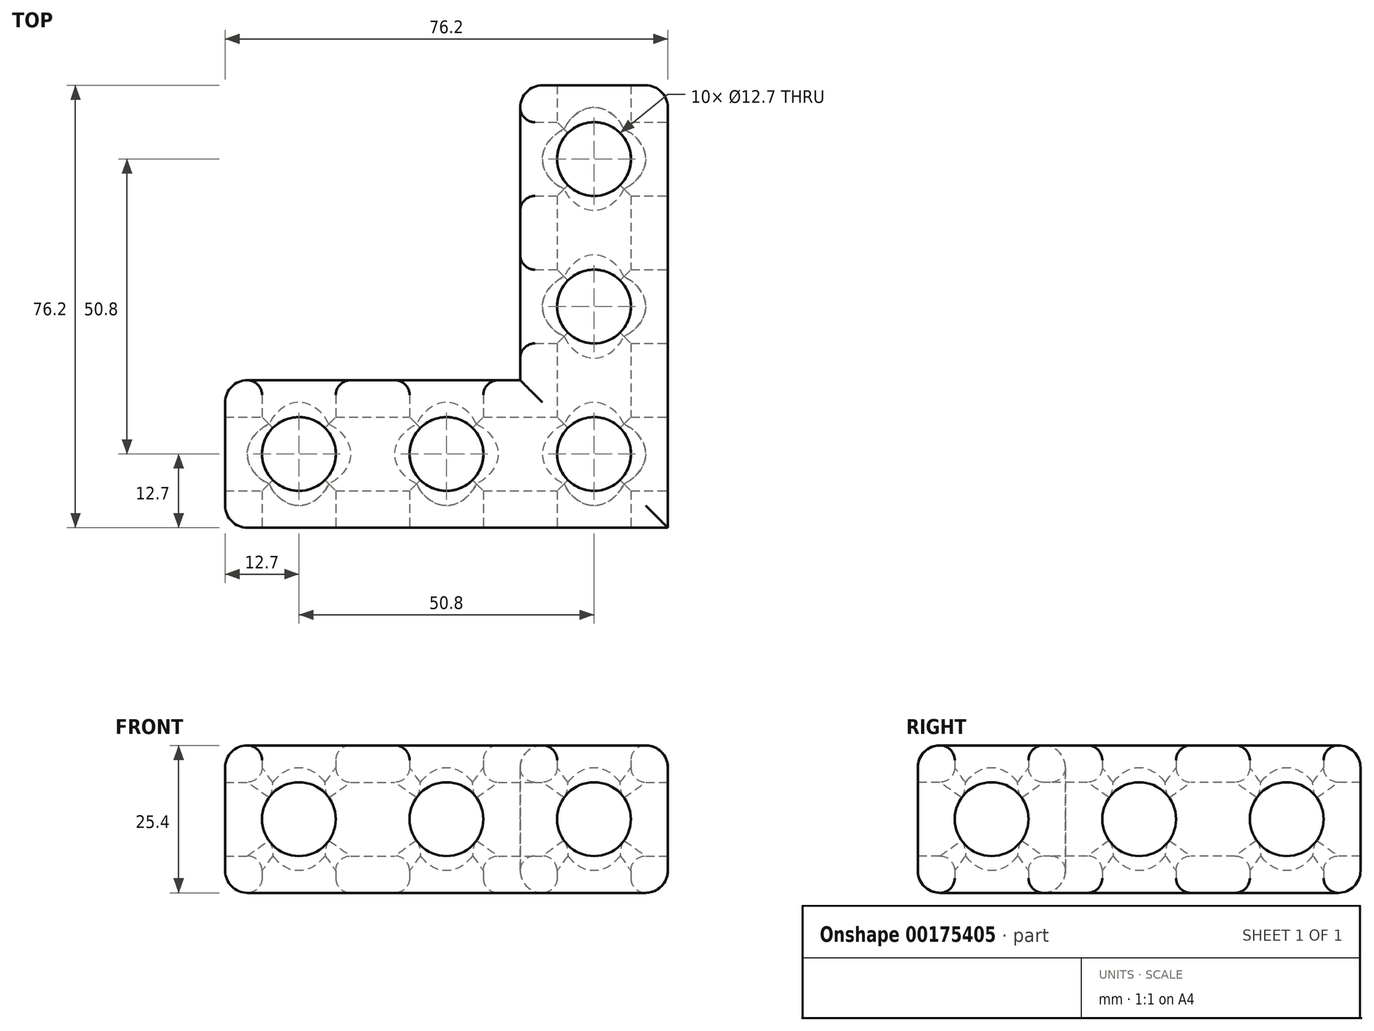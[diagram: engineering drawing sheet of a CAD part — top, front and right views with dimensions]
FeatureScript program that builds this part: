
annotation { "Feature Type Name" : "Feature", "Feature Type Description" : "" }
export const myFeature = defineFeature(function(context is Context, id is Id, definition is map)
    precondition{}
    {
        {
            var Q0;
            Q0=qCreatedBy(makeId("Top.planeOp"),FACE);
            var sketch = newSketch(context, id + "F0", { "sketchPlane" : qUnion([Q0])});
            skLineSegment(sketch, "E0.bottom", {"start": v(0, 0) * mm, "end": v(76.2, 0) * mm});
            skLineSegment(sketch, "E0.left", {"start": v(0, 0) * mm, "end": v(0, 25.4) * mm});
            skLineSegment(sketch, "E0.right", {"start": v(76.2, 0) * mm, "end": v(76.2, 18.8) * mm});
            skLineSegment(sketch, "E1.bottom", {"start": v(76.2, 0) * mm, "end": v(57.4, 0) * mm});
            skLineSegment(sketch, "E1.top", {"start": v(76.2, 76.2) * mm, "end": v(50.8, 76.2) * mm});
            skLineSegment(sketch, "E1.left", {"start": v(76.2, 0) * mm, "end": v(76.2, 76.2) * mm});
            skLineSegment(sketch, "E2", {"start": v(50.8, 76.2) * mm, "end": v(50.8, 25.4) * mm});
            skLineSegment(sketch, "E3", {"start": v(0, 25.4) * mm, "end": v(50.8, 25.4) * mm});
            skCircle(sketch, "E4", {"center": v(12.7, 12.7) * mm, "radius": 6.35 * mm});
            skCircle(sketch, "E5", {"center": v(38.1, 12.7) * mm, "radius": 6.35 * mm});
            skCircle(sketch, "E6", {"center": v(63.5, 12.7) * mm, "radius": 6.35 * mm});
            skCircle(sketch, "E7", {"center": v(63.5, 38.1) * mm, "radius": 6.35 * mm});
            skCircle(sketch, "E8", {"center": v(63.5, 63.5) * mm, "radius": 6.35 * mm});
            skSolve(sketch);
        }
        {
            var Q0;
            Q0=qSketchRegion(id+"F0",true);
            extrude(context, id + "F1", {"entities" : qUnion([Q0]), "depth" : 25.4 * mm});
        }
        {
            var Q0;
            Q0=makeQuery(id+"F1.opExtrude","SWEPT_FACE",FACE,{"disambiguationData":[OSD([sQuery(id+"F0.wireOp",EDGE,"E0.bottom"),sQuery(id+"F0.wireOp",EDGE,"E1.bottom")])]});
            var sketch = newSketch(context, id + "F2", { "sketchPlane" : qUnion([Q0])});
            skCircle(sketch, "E9", {"center": v(12.7, 12.7) * mm, "radius": 6.35 * mm});
            skCircle(sketch, "E10", {"center": v(38.1, 12.7) * mm, "radius": 6.35 * mm});
            skCircle(sketch, "E11", {"center": v(63.5, 12.7) * mm, "radius": 6.35 * mm});
            skSolve(sketch);
        }
        {
            var Q0;
            Q0=qSketchRegion(id+"F2",true);
            extrude(context, id + "F3", {"entities" : qUnion([Q0]), "operationType" : NewBodyOperationType.REMOVE, "oppositeDirection" : true, "depth" : 76.2 * mm});
        }
        {
            var Q0;
            Q0=makeQuery(id+"F1.opExtrude","SWEPT_FACE",FACE,{"disambiguationData":[OSD([sQuery(id+"F0.wireOp",EDGE,"E1.left")])]});
            var sketch = newSketch(context, id + "F4", { "sketchPlane" : qUnion([Q0])});
            skLineSegment(sketch, "E12.bottom", {"start": v(0, 0) * mm, "end": v(25.4, 0) * mm});
            skLineSegment(sketch, "E12.top", {"start": v(0, 25.4) * mm, "end": v(25.4, 25.4) * mm});
            skLineSegment(sketch, "E12.left", {"start": v(0, 0) * mm, "end": v(0, 25.4) * mm});
            skLineSegment(sketch, "E13.bottom", {"start": v(25.4, 0) * mm, "end": v(50.8, 0) * mm});
            skLineSegment(sketch, "E13.top", {"start": v(25.4, 25.4) * mm, "end": v(50.8, 25.4) * mm});
            skLineSegment(sketch, "E14.bottom", {"start": v(50.8, 0) * mm, "end": v(76.2, 0) * mm});
            skLineSegment(sketch, "E14.top", {"start": v(50.8, 25.4) * mm, "end": v(76.2, 25.4) * mm});
            skLineSegment(sketch, "E14.right", {"start": v(76.2, 0) * mm, "end": v(76.2, 25.4) * mm});
            skCircle(sketch, "E15", {"center": v(12.7, 12.7) * mm, "radius": 6.35 * mm});
            skCircle(sketch, "E16", {"center": v(38.1, 12.7) * mm, "radius": 6.35 * mm});
            skCircle(sketch, "E17", {"center": v(63.5, 12.7) * mm, "radius": 6.35 * mm});
            skSolve(sketch);
        }
        {
            var Q0;
            Q0=makeQuery(id+"F4.imprint","IMPRINT",FACE,{"disambiguationData":[TD([[makeQuery(id+"F4.imprint","IMPRINT",EDGE,{"derivedFrom":sQuery(id+"F4.wireOp",EDGE,"E15")}),1.0]])]});
            var Q1;
            Q1=makeQuery(id+"F4.imprint","IMPRINT",FACE,{"disambiguationData":[TD([[makeQuery(id+"F4.imprint","IMPRINT",EDGE,{"derivedFrom":sQuery(id+"F4.wireOp",EDGE,"E16")}),1.0]])]});
            var Q2;
            Q2=makeQuery(id+"F4.imprint","IMPRINT",FACE,{"disambiguationData":[TD([[makeQuery(id+"F4.imprint","IMPRINT",EDGE,{"derivedFrom":sQuery(id+"F4.wireOp",EDGE,"E17")}),1.0]])]});
            extrude(context, id + "F5", {"entities" : qUnion([Q0, Q1, Q2]), "operationType" : NewBodyOperationType.REMOVE, "oppositeDirection" : true, "depth" : 76.2 * mm});
        }
        {
            var Q0;
            Q0=makeQuery(id+"F1.opExtrude","CAP_EDGE",EDGE,{"disambiguationData":[OSD([sQuery(id+"F0.wireOp",EDGE,"E0.bottom"),sQuery(id+"F0.wireOp",EDGE,"E1.bottom")])],"isStart":false});
            var Q1;
            Q1=makeQuery(id+"F1.opExtrude","CAP_EDGE",EDGE,{"disambiguationData":[OSD([sQuery(id+"F0.wireOp",EDGE,"E1.left")])],"isStart":false});
            var Q2;
            Q2=makeQuery(id+"F1.opExtrude","CAP_EDGE",EDGE,{"disambiguationData":[OSD([sQuery(id+"F0.wireOp",EDGE,"E3")])],"isStart":false});
            var Q3;
            Q3=makeQuery(id+"F1.opExtrude","CAP_EDGE",EDGE,{"disambiguationData":[OSD([sQuery(id+"F0.wireOp",EDGE,"E2")])],"isStart":false});
            var Q4;
            Q4=makeQuery(id+"F1.opExtrude","SWEPT_EDGE",EDGE,{"disambiguationData":[OSD([sQuery(id+"F0.wireOp",EDGE,"E0.bottom"),sQuery(id+"F0.wireOp",EDGE,"E0.left")])]});
            var Q5;
            Q5=makeQuery(id+"F1.opExtrude","CAP_EDGE",EDGE,{"disambiguationData":[OSD([sQuery(id+"F0.wireOp",EDGE,"E0.bottom"),sQuery(id+"F0.wireOp",EDGE,"E1.bottom")])],"isStart":true});
            var Q6;
            Q6=makeQuery(id+"F1.opExtrude","CAP_EDGE",EDGE,{"disambiguationData":[OSD([sQuery(id+"F0.wireOp",EDGE,"E1.left")])],"isStart":true});
            var Q7;
            Q7=makeQuery(id+"F1.opExtrude","SWEPT_EDGE",EDGE,{"disambiguationData":[OSD([sQuery(id+"F0.wireOp",EDGE,"E1.bottom"),sQuery(id+"F0.wireOp",EDGE,"E1.left")])]});
            var Q8;
            Q8=makeQuery(id+"F1.opExtrude","CAP_EDGE",EDGE,{"disambiguationData":[OSD([sQuery(id+"F0.wireOp",EDGE,"E0.left")])],"isStart":false});
            var Q9;
            Q9=makeQuery(id+"F1.opExtrude","CAP_EDGE",EDGE,{"disambiguationData":[OSD([sQuery(id+"F0.wireOp",EDGE,"E0.left")])],"isStart":true});
            var Q10;
            Q10=makeQuery(id+"F1.opExtrude","SWEPT_EDGE",EDGE,{"disambiguationData":[OSD([sQuery(id+"F0.wireOp",EDGE,"E0.left"),sQuery(id+"F0.wireOp",EDGE,"E3")])]});
            var Q11;
            Q11=makeQuery(id+"F1.opExtrude","CAP_EDGE",EDGE,{"disambiguationData":[OSD([sQuery(id+"F0.wireOp",EDGE,"E3")])],"isStart":true});
            var Q12;
            Q12=makeQuery(id+"F1.opExtrude","SWEPT_EDGE",EDGE,{"disambiguationData":[OSD([sQuery(id+"F0.wireOp",EDGE,"E1.top"),sQuery(id+"F0.wireOp",EDGE,"E2")])]});
            var Q13;
            Q13=makeQuery(id+"F1.opExtrude","CAP_EDGE",EDGE,{"disambiguationData":[OSD([sQuery(id+"F0.wireOp",EDGE,"E2")])],"isStart":true});
            var Q14;
            Q14=makeQuery(id+"F1.opExtrude","CAP_EDGE",EDGE,{"disambiguationData":[OSD([sQuery(id+"F0.wireOp",EDGE,"E1.top")])],"isStart":true});
            var Q15;
            Q15=makeQuery(id+"F1.opExtrude","SWEPT_EDGE",EDGE,{"disambiguationData":[OSD([sQuery(id+"F0.wireOp",EDGE,"E1.top"),sQuery(id+"F0.wireOp",EDGE,"E1.left")])]});
            var Q16;
            Q16=makeQuery(id+"F1.opExtrude","CAP_EDGE",EDGE,{"disambiguationData":[OSD([sQuery(id+"F0.wireOp",EDGE,"E1.top")])],"isStart":false});
            fillet(context, id + "F6", {"entities" : qUnion([Q0, Q1, Q2, Q3, Q4, Q5, Q6, Q7, Q8, Q9, Q10, Q11, Q12, Q13, Q14, Q15, Q16]), "radius" : 3.8 * mm, "allowEdgeOverflow" : false});
        }
        {
            var Q0;
            {var subQ0=sQuery(id+"F0.wireOp",EDGE,"E4");var subQ1=makeQuery(id+"F1.opExtrude","SWEPT_FACE",FACE,{"disambiguationData":[OSD([subQ0])]});Q0=makeQuery(id+"F5.boolean.opBoolean","INTERSECT",EDGE,{"disambiguationData":[OD(0.0)],"derivedFrom":[makeQuery(id+"F3.boolean.opBoolean","SPLIT",FACE,{"disambiguationData":[TD([makeQuery(id+"F1.opExtrude","CAP_FACE",FACE,{"disambiguationData":[OSD([sQuery(id+"F0.wireOp",EDGE,"E0.bottom"),sQuery(id+"F0.wireOp",EDGE,"E0.left"),sQuery(id+"F0.wireOp",EDGE,"E1.bottom"),sQuery(id+"F0.wireOp",EDGE,"E1.top"),sQuery(id+"F0.wireOp",EDGE,"E1.left"),sQuery(id+"F0.wireOp",EDGE,"E2"),sQuery(id+"F0.wireOp",EDGE,"E3"),subQ0,sQuery(id+"F0.wireOp",EDGE,"E5"),sQuery(id+"F0.wireOp",EDGE,"E6"),sQuery(id+"F0.wireOp",EDGE,"E7"),sQuery(id+"F0.wireOp",EDGE,"E8")])],"isStart":true})])],"derivedFrom":subQ1}),makeQuery(id+"F5.opExtrude","SWEPT_FACE",FACE,{"disambiguationData":[OSD([sQuery(id+"F4.wireOp",EDGE,"E15")])]})]});}
            var Q1;
            Q1=makeQuery(id+"F3.boolean.opBoolean","INTERSECT",EDGE,{"disambiguationData":[OD(0.0)],"derivedFrom":[makeQuery(id+"F1.opExtrude","SWEPT_FACE",FACE,{"disambiguationData":[OSD([sQuery(id+"F0.wireOp",EDGE,"E4")])]}),makeQuery(id+"F3.opExtrude","SWEPT_FACE",FACE,{"disambiguationData":[OSD([sQuery(id+"F2.wireOp",EDGE,"E9")])]})]});
            var Q2;
            Q2=makeQuery(id+"F5.boolean.opBoolean","INTERSECT",EDGE,{"disambiguationData":[OD(0.0)],"derivedFrom":[makeQuery(id+"F3.boolean.opBoolean","COPY",FACE,{"disambiguationData":[OD(0.0)],"derivedFrom":makeQuery(id+"F3.opExtrude","SWEPT_FACE",FACE,{"disambiguationData":[OSD([sQuery(id+"F2.wireOp",EDGE,"E9")])]})}),makeQuery(id+"F5.opExtrude","SWEPT_FACE",FACE,{"disambiguationData":[OSD([sQuery(id+"F4.wireOp",EDGE,"E15")])]})]});
            var Q3;
            Q3=makeQuery(id+"F5.boolean.opBoolean","INTERSECT",EDGE,{"disambiguationData":[OD(0.0)],"derivedFrom":[makeQuery(id+"F3.boolean.opBoolean","COPY",FACE,{"disambiguationData":[OD(1.0)],"derivedFrom":makeQuery(id+"F3.opExtrude","SWEPT_FACE",FACE,{"disambiguationData":[OSD([sQuery(id+"F2.wireOp",EDGE,"E9")])]})}),makeQuery(id+"F5.opExtrude","SWEPT_FACE",FACE,{"disambiguationData":[OSD([sQuery(id+"F4.wireOp",EDGE,"E15")])]})]});
            var Q4;
            {var subQ0=sQuery(id+"F0.wireOp",EDGE,"E4");var subQ1=makeQuery(id+"F1.opExtrude","SWEPT_FACE",FACE,{"disambiguationData":[OSD([subQ0])]});Q4=makeQuery(id+"F5.boolean.opBoolean","INTERSECT",EDGE,{"disambiguationData":[OD(0.0)],"derivedFrom":[makeQuery(id+"F3.boolean.opBoolean","SPLIT",FACE,{"disambiguationData":[TD([makeQuery(id+"F1.opExtrude","CAP_FACE",FACE,{"disambiguationData":[OSD([sQuery(id+"F0.wireOp",EDGE,"E0.bottom"),sQuery(id+"F0.wireOp",EDGE,"E0.left"),sQuery(id+"F0.wireOp",EDGE,"E1.bottom"),sQuery(id+"F0.wireOp",EDGE,"E1.top"),sQuery(id+"F0.wireOp",EDGE,"E1.left"),sQuery(id+"F0.wireOp",EDGE,"E2"),sQuery(id+"F0.wireOp",EDGE,"E3"),subQ0,sQuery(id+"F0.wireOp",EDGE,"E5"),sQuery(id+"F0.wireOp",EDGE,"E6"),sQuery(id+"F0.wireOp",EDGE,"E7"),sQuery(id+"F0.wireOp",EDGE,"E8")])],"isStart":false})])],"derivedFrom":subQ1}),makeQuery(id+"F5.opExtrude","SWEPT_FACE",FACE,{"disambiguationData":[OSD([sQuery(id+"F4.wireOp",EDGE,"E15")])]})]});}
            var Q5;
            Q5=makeQuery(id+"F3.boolean.opBoolean","INTERSECT",EDGE,{"disambiguationData":[OD(3.0)],"derivedFrom":[makeQuery(id+"F1.opExtrude","SWEPT_FACE",FACE,{"disambiguationData":[OSD([sQuery(id+"F0.wireOp",EDGE,"E4")])]}),makeQuery(id+"F3.opExtrude","SWEPT_FACE",FACE,{"disambiguationData":[OSD([sQuery(id+"F2.wireOp",EDGE,"E9")])]})]});
            var Q6;
            Q6=makeQuery(id+"F3.boolean.opBoolean","INTERSECT",EDGE,{"disambiguationData":[OD(1.0)],"derivedFrom":[makeQuery(id+"F1.opExtrude","SWEPT_FACE",FACE,{"disambiguationData":[OSD([sQuery(id+"F0.wireOp",EDGE,"E4")])]}),makeQuery(id+"F3.opExtrude","SWEPT_FACE",FACE,{"disambiguationData":[OSD([sQuery(id+"F2.wireOp",EDGE,"E9")])]})]});
            var Q7;
            {var subQ0=sQuery(id+"F0.wireOp",EDGE,"E4");var subQ1=makeQuery(id+"F1.opExtrude","SWEPT_FACE",FACE,{"disambiguationData":[OSD([subQ0])]});Q7=makeQuery(id+"F5.boolean.opBoolean","INTERSECT",EDGE,{"disambiguationData":[OD(1.0)],"derivedFrom":[makeQuery(id+"F3.boolean.opBoolean","SPLIT",FACE,{"disambiguationData":[TD([makeQuery(id+"F1.opExtrude","CAP_FACE",FACE,{"disambiguationData":[OSD([sQuery(id+"F0.wireOp",EDGE,"E0.bottom"),sQuery(id+"F0.wireOp",EDGE,"E0.left"),sQuery(id+"F0.wireOp",EDGE,"E1.bottom"),sQuery(id+"F0.wireOp",EDGE,"E1.top"),sQuery(id+"F0.wireOp",EDGE,"E1.left"),sQuery(id+"F0.wireOp",EDGE,"E2"),sQuery(id+"F0.wireOp",EDGE,"E3"),subQ0,sQuery(id+"F0.wireOp",EDGE,"E5"),sQuery(id+"F0.wireOp",EDGE,"E6"),sQuery(id+"F0.wireOp",EDGE,"E7"),sQuery(id+"F0.wireOp",EDGE,"E8")])],"isStart":true})])],"derivedFrom":subQ1}),makeQuery(id+"F5.opExtrude","SWEPT_FACE",FACE,{"disambiguationData":[OSD([sQuery(id+"F4.wireOp",EDGE,"E15")])]})]});}
            var Q8;
            Q8=makeQuery(id+"F5.boolean.opBoolean","INTERSECT",EDGE,{"disambiguationData":[OD(1.0)],"derivedFrom":[makeQuery(id+"F3.boolean.opBoolean","COPY",FACE,{"disambiguationData":[OD(0.0)],"derivedFrom":makeQuery(id+"F3.opExtrude","SWEPT_FACE",FACE,{"disambiguationData":[OSD([sQuery(id+"F2.wireOp",EDGE,"E9")])]})}),makeQuery(id+"F5.opExtrude","SWEPT_FACE",FACE,{"disambiguationData":[OSD([sQuery(id+"F4.wireOp",EDGE,"E15")])]})]});
            var Q9;
            Q9=makeQuery(id+"F3.boolean.opBoolean","INTERSECT",EDGE,{"disambiguationData":[OD(2.0)],"derivedFrom":[makeQuery(id+"F1.opExtrude","SWEPT_FACE",FACE,{"disambiguationData":[OSD([sQuery(id+"F0.wireOp",EDGE,"E4")])]}),makeQuery(id+"F3.opExtrude","SWEPT_FACE",FACE,{"disambiguationData":[OSD([sQuery(id+"F2.wireOp",EDGE,"E9")])]})]});
            var Q10;
            {var subQ0=sQuery(id+"F0.wireOp",EDGE,"E4");var subQ1=makeQuery(id+"F1.opExtrude","SWEPT_FACE",FACE,{"disambiguationData":[OSD([subQ0])]});Q10=makeQuery(id+"F5.boolean.opBoolean","INTERSECT",EDGE,{"disambiguationData":[OD(1.0)],"derivedFrom":[makeQuery(id+"F3.boolean.opBoolean","SPLIT",FACE,{"disambiguationData":[TD([makeQuery(id+"F1.opExtrude","CAP_FACE",FACE,{"disambiguationData":[OSD([sQuery(id+"F0.wireOp",EDGE,"E0.bottom"),sQuery(id+"F0.wireOp",EDGE,"E0.left"),sQuery(id+"F0.wireOp",EDGE,"E1.bottom"),sQuery(id+"F0.wireOp",EDGE,"E1.top"),sQuery(id+"F0.wireOp",EDGE,"E1.left"),sQuery(id+"F0.wireOp",EDGE,"E2"),sQuery(id+"F0.wireOp",EDGE,"E3"),subQ0,sQuery(id+"F0.wireOp",EDGE,"E5"),sQuery(id+"F0.wireOp",EDGE,"E6"),sQuery(id+"F0.wireOp",EDGE,"E7"),sQuery(id+"F0.wireOp",EDGE,"E8")])],"isStart":false})])],"derivedFrom":subQ1}),makeQuery(id+"F5.opExtrude","SWEPT_FACE",FACE,{"disambiguationData":[OSD([sQuery(id+"F4.wireOp",EDGE,"E15")])]})]});}
            var Q11;
            Q11=makeQuery(id+"F5.boolean.opBoolean","INTERSECT",EDGE,{"disambiguationData":[OD(1.0)],"derivedFrom":[makeQuery(id+"F3.boolean.opBoolean","COPY",FACE,{"disambiguationData":[OD(1.0)],"derivedFrom":makeQuery(id+"F3.opExtrude","SWEPT_FACE",FACE,{"disambiguationData":[OSD([sQuery(id+"F2.wireOp",EDGE,"E9")])]})}),makeQuery(id+"F5.opExtrude","SWEPT_FACE",FACE,{"disambiguationData":[OSD([sQuery(id+"F4.wireOp",EDGE,"E15")])]})]});
            fillet(context, id + "F7", {"entities" : qUnion([Q0, Q1, Q2, Q3, Q4, Q5, Q6, Q7, Q8, Q9, Q10, Q11]), "radius" : 2.54 * mm, "tangentPropagation" : true, "allowEdgeOverflow" : false});
        }
        {
            var Q0;
            {var subQ0=sQuery(id+"F0.wireOp",EDGE,"E5");var subQ1=makeQuery(id+"F1.opExtrude","SWEPT_FACE",FACE,{"disambiguationData":[OSD([subQ0])]});Q0=makeQuery(id+"F5.boolean.opBoolean","INTERSECT",EDGE,{"disambiguationData":[OD(0.0)],"derivedFrom":[makeQuery(id+"F3.boolean.opBoolean","SPLIT",FACE,{"disambiguationData":[TD([makeQuery(id+"F1.opExtrude","CAP_FACE",FACE,{"disambiguationData":[OSD([sQuery(id+"F0.wireOp",EDGE,"E0.bottom"),sQuery(id+"F0.wireOp",EDGE,"E0.left"),sQuery(id+"F0.wireOp",EDGE,"E1.bottom"),sQuery(id+"F0.wireOp",EDGE,"E1.top"),sQuery(id+"F0.wireOp",EDGE,"E1.left"),sQuery(id+"F0.wireOp",EDGE,"E2"),sQuery(id+"F0.wireOp",EDGE,"E3"),sQuery(id+"F0.wireOp",EDGE,"E4"),subQ0,sQuery(id+"F0.wireOp",EDGE,"E6"),sQuery(id+"F0.wireOp",EDGE,"E7"),sQuery(id+"F0.wireOp",EDGE,"E8")])],"isStart":true})])],"derivedFrom":subQ1}),makeQuery(id+"F5.opExtrude","SWEPT_FACE",FACE,{"disambiguationData":[OSD([sQuery(id+"F4.wireOp",EDGE,"E15")])]})]});}
            var Q1;
            Q1=makeQuery(id+"F3.boolean.opBoolean","INTERSECT",EDGE,{"disambiguationData":[OD(0.0)],"derivedFrom":[makeQuery(id+"F1.opExtrude","SWEPT_FACE",FACE,{"disambiguationData":[OSD([sQuery(id+"F0.wireOp",EDGE,"E5")])]}),makeQuery(id+"F3.opExtrude","SWEPT_FACE",FACE,{"disambiguationData":[OSD([sQuery(id+"F2.wireOp",EDGE,"E10")])]})]});
            var Q2;
            Q2=makeQuery(id+"F3.boolean.opBoolean","INTERSECT",EDGE,{"disambiguationData":[OD(1.0)],"derivedFrom":[makeQuery(id+"F1.opExtrude","SWEPT_FACE",FACE,{"disambiguationData":[OSD([sQuery(id+"F0.wireOp",EDGE,"E5")])]}),makeQuery(id+"F3.opExtrude","SWEPT_FACE",FACE,{"disambiguationData":[OSD([sQuery(id+"F2.wireOp",EDGE,"E10")])]})]});
            var Q3;
            {var subQ0=sQuery(id+"F0.wireOp",EDGE,"E5");var subQ1=makeQuery(id+"F1.opExtrude","SWEPT_FACE",FACE,{"disambiguationData":[OSD([subQ0])]});Q3=makeQuery(id+"F5.boolean.opBoolean","INTERSECT",EDGE,{"disambiguationData":[OD(1.0)],"derivedFrom":[makeQuery(id+"F3.boolean.opBoolean","SPLIT",FACE,{"disambiguationData":[TD([makeQuery(id+"F1.opExtrude","CAP_FACE",FACE,{"disambiguationData":[OSD([sQuery(id+"F0.wireOp",EDGE,"E0.bottom"),sQuery(id+"F0.wireOp",EDGE,"E0.left"),sQuery(id+"F0.wireOp",EDGE,"E1.bottom"),sQuery(id+"F0.wireOp",EDGE,"E1.top"),sQuery(id+"F0.wireOp",EDGE,"E1.left"),sQuery(id+"F0.wireOp",EDGE,"E2"),sQuery(id+"F0.wireOp",EDGE,"E3"),sQuery(id+"F0.wireOp",EDGE,"E4"),subQ0,sQuery(id+"F0.wireOp",EDGE,"E6"),sQuery(id+"F0.wireOp",EDGE,"E7"),sQuery(id+"F0.wireOp",EDGE,"E8")])],"isStart":true})])],"derivedFrom":subQ1}),makeQuery(id+"F5.opExtrude","SWEPT_FACE",FACE,{"disambiguationData":[OSD([sQuery(id+"F4.wireOp",EDGE,"E15")])]})]});}
            var Q4;
            Q4=makeQuery(id+"F5.boolean.opBoolean","INTERSECT",EDGE,{"disambiguationData":[OD(0.0)],"derivedFrom":[makeQuery(id+"F3.boolean.opBoolean","COPY",FACE,{"disambiguationData":[OD(0.0)],"derivedFrom":makeQuery(id+"F3.opExtrude","SWEPT_FACE",FACE,{"disambiguationData":[OSD([sQuery(id+"F2.wireOp",EDGE,"E10")])]})}),makeQuery(id+"F5.opExtrude","SWEPT_FACE",FACE,{"disambiguationData":[OSD([sQuery(id+"F4.wireOp",EDGE,"E15")])]})]});
            var Q5;
            Q5=makeQuery(id+"F5.boolean.opBoolean","INTERSECT",EDGE,{"disambiguationData":[OD(0.0)],"derivedFrom":[makeQuery(id+"F3.boolean.opBoolean","COPY",FACE,{"disambiguationData":[OD(1.0)],"derivedFrom":makeQuery(id+"F3.opExtrude","SWEPT_FACE",FACE,{"disambiguationData":[OSD([sQuery(id+"F2.wireOp",EDGE,"E10")])]})}),makeQuery(id+"F5.opExtrude","SWEPT_FACE",FACE,{"disambiguationData":[OSD([sQuery(id+"F4.wireOp",EDGE,"E15")])]})]});
            var Q6;
            Q6=makeQuery(id+"F5.boolean.opBoolean","INTERSECT",EDGE,{"disambiguationData":[OD(1.0)],"derivedFrom":[makeQuery(id+"F3.boolean.opBoolean","COPY",FACE,{"disambiguationData":[OD(1.0)],"derivedFrom":makeQuery(id+"F3.opExtrude","SWEPT_FACE",FACE,{"disambiguationData":[OSD([sQuery(id+"F2.wireOp",EDGE,"E10")])]})}),makeQuery(id+"F5.opExtrude","SWEPT_FACE",FACE,{"disambiguationData":[OSD([sQuery(id+"F4.wireOp",EDGE,"E15")])]})]});
            var Q7;
            Q7=makeQuery(id+"F5.boolean.opBoolean","INTERSECT",EDGE,{"disambiguationData":[OD(1.0)],"derivedFrom":[makeQuery(id+"F3.boolean.opBoolean","COPY",FACE,{"disambiguationData":[OD(0.0)],"derivedFrom":makeQuery(id+"F3.opExtrude","SWEPT_FACE",FACE,{"disambiguationData":[OSD([sQuery(id+"F2.wireOp",EDGE,"E10")])]})}),makeQuery(id+"F5.opExtrude","SWEPT_FACE",FACE,{"disambiguationData":[OSD([sQuery(id+"F4.wireOp",EDGE,"E15")])]})]});
            var Q8;
            Q8=makeQuery(id+"F3.boolean.opBoolean","INTERSECT",EDGE,{"disambiguationData":[OD(2.0)],"derivedFrom":[makeQuery(id+"F1.opExtrude","SWEPT_FACE",FACE,{"disambiguationData":[OSD([sQuery(id+"F0.wireOp",EDGE,"E5")])]}),makeQuery(id+"F3.opExtrude","SWEPT_FACE",FACE,{"disambiguationData":[OSD([sQuery(id+"F2.wireOp",EDGE,"E10")])]})]});
            var Q9;
            {var subQ0=sQuery(id+"F0.wireOp",EDGE,"E5");var subQ1=makeQuery(id+"F1.opExtrude","SWEPT_FACE",FACE,{"disambiguationData":[OSD([subQ0])]});Q9=makeQuery(id+"F5.boolean.opBoolean","INTERSECT",EDGE,{"disambiguationData":[OD(0.0)],"derivedFrom":[makeQuery(id+"F3.boolean.opBoolean","SPLIT",FACE,{"disambiguationData":[TD([makeQuery(id+"F1.opExtrude","CAP_FACE",FACE,{"disambiguationData":[OSD([sQuery(id+"F0.wireOp",EDGE,"E0.bottom"),sQuery(id+"F0.wireOp",EDGE,"E0.left"),sQuery(id+"F0.wireOp",EDGE,"E1.bottom"),sQuery(id+"F0.wireOp",EDGE,"E1.top"),sQuery(id+"F0.wireOp",EDGE,"E1.left"),sQuery(id+"F0.wireOp",EDGE,"E2"),sQuery(id+"F0.wireOp",EDGE,"E3"),sQuery(id+"F0.wireOp",EDGE,"E4"),subQ0,sQuery(id+"F0.wireOp",EDGE,"E6"),sQuery(id+"F0.wireOp",EDGE,"E7"),sQuery(id+"F0.wireOp",EDGE,"E8")])],"isStart":false})])],"derivedFrom":subQ1}),makeQuery(id+"F5.opExtrude","SWEPT_FACE",FACE,{"disambiguationData":[OSD([sQuery(id+"F4.wireOp",EDGE,"E15")])]})]});}
            var Q10;
            Q10=makeQuery(id+"F3.boolean.opBoolean","INTERSECT",EDGE,{"disambiguationData":[OD(3.0)],"derivedFrom":[makeQuery(id+"F1.opExtrude","SWEPT_FACE",FACE,{"disambiguationData":[OSD([sQuery(id+"F0.wireOp",EDGE,"E5")])]}),makeQuery(id+"F3.opExtrude","SWEPT_FACE",FACE,{"disambiguationData":[OSD([sQuery(id+"F2.wireOp",EDGE,"E10")])]})]});
            var Q11;
            {var subQ0=sQuery(id+"F0.wireOp",EDGE,"E5");var subQ1=makeQuery(id+"F1.opExtrude","SWEPT_FACE",FACE,{"disambiguationData":[OSD([subQ0])]});Q11=makeQuery(id+"F5.boolean.opBoolean","INTERSECT",EDGE,{"disambiguationData":[OD(1.0)],"derivedFrom":[makeQuery(id+"F3.boolean.opBoolean","SPLIT",FACE,{"disambiguationData":[TD([makeQuery(id+"F1.opExtrude","CAP_FACE",FACE,{"disambiguationData":[OSD([sQuery(id+"F0.wireOp",EDGE,"E0.bottom"),sQuery(id+"F0.wireOp",EDGE,"E0.left"),sQuery(id+"F0.wireOp",EDGE,"E1.bottom"),sQuery(id+"F0.wireOp",EDGE,"E1.top"),sQuery(id+"F0.wireOp",EDGE,"E1.left"),sQuery(id+"F0.wireOp",EDGE,"E2"),sQuery(id+"F0.wireOp",EDGE,"E3"),sQuery(id+"F0.wireOp",EDGE,"E4"),subQ0,sQuery(id+"F0.wireOp",EDGE,"E6"),sQuery(id+"F0.wireOp",EDGE,"E7"),sQuery(id+"F0.wireOp",EDGE,"E8")])],"isStart":false})])],"derivedFrom":subQ1}),makeQuery(id+"F5.opExtrude","SWEPT_FACE",FACE,{"disambiguationData":[OSD([sQuery(id+"F4.wireOp",EDGE,"E15")])]})]});}
            var Q12;
            Q12=makeQuery(id+"F5.boolean.opBoolean","INTERSECT",EDGE,{"disambiguationData":[OD(1.0)],"derivedFrom":[makeQuery(id+"F3.boolean.opBoolean","COPY",FACE,{"disambiguationData":[OD(2.0)],"derivedFrom":makeQuery(id+"F3.opExtrude","SWEPT_FACE",FACE,{"disambiguationData":[OSD([sQuery(id+"F2.wireOp",EDGE,"E11")])]})}),makeQuery(id+"F5.opExtrude","SWEPT_FACE",FACE,{"disambiguationData":[OSD([sQuery(id+"F4.wireOp",EDGE,"E15")])]})]});
            var Q13;
            {var subQ0=sQuery(id+"F0.wireOp",EDGE,"E6");var subQ1=makeQuery(id+"F1.opExtrude","SWEPT_FACE",FACE,{"disambiguationData":[OSD([subQ0])]});Q13=makeQuery(id+"F5.boolean.opBoolean","INTERSECT",EDGE,{"disambiguationData":[OD(1.0)],"derivedFrom":[makeQuery(id+"F3.boolean.opBoolean","SPLIT",FACE,{"disambiguationData":[TD([makeQuery(id+"F1.opExtrude","CAP_FACE",FACE,{"disambiguationData":[OSD([sQuery(id+"F0.wireOp",EDGE,"E0.bottom"),sQuery(id+"F0.wireOp",EDGE,"E0.left"),sQuery(id+"F0.wireOp",EDGE,"E1.bottom"),sQuery(id+"F0.wireOp",EDGE,"E1.top"),sQuery(id+"F0.wireOp",EDGE,"E1.left"),sQuery(id+"F0.wireOp",EDGE,"E2"),sQuery(id+"F0.wireOp",EDGE,"E3"),sQuery(id+"F0.wireOp",EDGE,"E4"),sQuery(id+"F0.wireOp",EDGE,"E5"),subQ0,sQuery(id+"F0.wireOp",EDGE,"E7"),sQuery(id+"F0.wireOp",EDGE,"E8")])],"isStart":true})])],"derivedFrom":subQ1}),makeQuery(id+"F5.opExtrude","SWEPT_FACE",FACE,{"disambiguationData":[OSD([sQuery(id+"F4.wireOp",EDGE,"E15")])]})]});}
            var Q14;
            Q14=makeQuery(id+"F3.boolean.opBoolean","INTERSECT",EDGE,{"disambiguationData":[OD(2.0)],"derivedFrom":[makeQuery(id+"F1.opExtrude","SWEPT_FACE",FACE,{"disambiguationData":[OSD([sQuery(id+"F0.wireOp",EDGE,"E6")])]}),makeQuery(id+"F3.opExtrude","SWEPT_FACE",FACE,{"disambiguationData":[OSD([sQuery(id+"F2.wireOp",EDGE,"E11")])]})]});
            var Q15;
            {var subQ0=sQuery(id+"F0.wireOp",EDGE,"E6");var subQ1=makeQuery(id+"F1.opExtrude","SWEPT_FACE",FACE,{"disambiguationData":[OSD([subQ0])]});Q15=makeQuery(id+"F5.boolean.opBoolean","INTERSECT",EDGE,{"disambiguationData":[OD(1.0)],"derivedFrom":[makeQuery(id+"F3.boolean.opBoolean","SPLIT",FACE,{"disambiguationData":[TD([makeQuery(id+"F1.opExtrude","CAP_FACE",FACE,{"disambiguationData":[OSD([sQuery(id+"F0.wireOp",EDGE,"E0.bottom"),sQuery(id+"F0.wireOp",EDGE,"E0.left"),sQuery(id+"F0.wireOp",EDGE,"E1.bottom"),sQuery(id+"F0.wireOp",EDGE,"E1.top"),sQuery(id+"F0.wireOp",EDGE,"E1.left"),sQuery(id+"F0.wireOp",EDGE,"E2"),sQuery(id+"F0.wireOp",EDGE,"E3"),sQuery(id+"F0.wireOp",EDGE,"E4"),sQuery(id+"F0.wireOp",EDGE,"E5"),subQ0,sQuery(id+"F0.wireOp",EDGE,"E7"),sQuery(id+"F0.wireOp",EDGE,"E8")])],"isStart":false})])],"derivedFrom":subQ1}),makeQuery(id+"F5.opExtrude","SWEPT_FACE",FACE,{"disambiguationData":[OSD([sQuery(id+"F4.wireOp",EDGE,"E15")])]})]});}
            var Q16;
            Q16=makeQuery(id+"F3.boolean.opBoolean","INTERSECT",EDGE,{"disambiguationData":[OD(3.0)],"derivedFrom":[makeQuery(id+"F1.opExtrude","SWEPT_FACE",FACE,{"disambiguationData":[OSD([sQuery(id+"F0.wireOp",EDGE,"E6")])]}),makeQuery(id+"F3.opExtrude","SWEPT_FACE",FACE,{"disambiguationData":[OSD([sQuery(id+"F2.wireOp",EDGE,"E11")])]})]});
            var Q17;
            Q17=makeQuery(id+"F3.boolean.opBoolean","INTERSECT",EDGE,{"disambiguationData":[OD(0.0)],"derivedFrom":[makeQuery(id+"F1.opExtrude","SWEPT_FACE",FACE,{"disambiguationData":[OSD([sQuery(id+"F0.wireOp",EDGE,"E6")])]}),makeQuery(id+"F3.opExtrude","SWEPT_FACE",FACE,{"disambiguationData":[OSD([sQuery(id+"F2.wireOp",EDGE,"E11")])]})]});
            var Q18;
            Q18=makeQuery(id+"F5.boolean.opBoolean","INTERSECT",EDGE,{"disambiguationData":[OD(0.0)],"derivedFrom":[makeQuery(id+"F3.boolean.opBoolean","COPY",FACE,{"disambiguationData":[OD(0.0)],"derivedFrom":makeQuery(id+"F3.opExtrude","SWEPT_FACE",FACE,{"disambiguationData":[OSD([sQuery(id+"F2.wireOp",EDGE,"E11")])]})}),makeQuery(id+"F5.opExtrude","SWEPT_FACE",FACE,{"disambiguationData":[OSD([sQuery(id+"F4.wireOp",EDGE,"E15")])]})]});
            var Q19;
            Q19=makeQuery(id+"F3.boolean.opBoolean","INTERSECT",EDGE,{"disambiguationData":[OD(1.0)],"derivedFrom":[makeQuery(id+"F1.opExtrude","SWEPT_FACE",FACE,{"disambiguationData":[OSD([sQuery(id+"F0.wireOp",EDGE,"E6")])]}),makeQuery(id+"F3.opExtrude","SWEPT_FACE",FACE,{"disambiguationData":[OSD([sQuery(id+"F2.wireOp",EDGE,"E11")])]})]});
            var Q20;
            {var subQ0=sQuery(id+"F0.wireOp",EDGE,"E6");var subQ1=makeQuery(id+"F1.opExtrude","SWEPT_FACE",FACE,{"disambiguationData":[OSD([subQ0])]});Q20=makeQuery(id+"F5.boolean.opBoolean","INTERSECT",EDGE,{"disambiguationData":[OD(0.0)],"derivedFrom":[makeQuery(id+"F3.boolean.opBoolean","SPLIT",FACE,{"disambiguationData":[TD([makeQuery(id+"F1.opExtrude","CAP_FACE",FACE,{"disambiguationData":[OSD([sQuery(id+"F0.wireOp",EDGE,"E0.bottom"),sQuery(id+"F0.wireOp",EDGE,"E0.left"),sQuery(id+"F0.wireOp",EDGE,"E1.bottom"),sQuery(id+"F0.wireOp",EDGE,"E1.top"),sQuery(id+"F0.wireOp",EDGE,"E1.left"),sQuery(id+"F0.wireOp",EDGE,"E2"),sQuery(id+"F0.wireOp",EDGE,"E3"),sQuery(id+"F0.wireOp",EDGE,"E4"),sQuery(id+"F0.wireOp",EDGE,"E5"),subQ0,sQuery(id+"F0.wireOp",EDGE,"E7"),sQuery(id+"F0.wireOp",EDGE,"E8")])],"isStart":false})])],"derivedFrom":subQ1}),makeQuery(id+"F5.opExtrude","SWEPT_FACE",FACE,{"disambiguationData":[OSD([sQuery(id+"F4.wireOp",EDGE,"E15")])]})]});}
            var Q21;
            {var subQ0=sQuery(id+"F0.wireOp",EDGE,"E6");var subQ1=makeQuery(id+"F1.opExtrude","SWEPT_FACE",FACE,{"disambiguationData":[OSD([subQ0])]});Q21=makeQuery(id+"F5.boolean.opBoolean","INTERSECT",EDGE,{"disambiguationData":[OD(0.0)],"derivedFrom":[makeQuery(id+"F3.boolean.opBoolean","SPLIT",FACE,{"disambiguationData":[TD([makeQuery(id+"F1.opExtrude","CAP_FACE",FACE,{"disambiguationData":[OSD([sQuery(id+"F0.wireOp",EDGE,"E0.bottom"),sQuery(id+"F0.wireOp",EDGE,"E0.left"),sQuery(id+"F0.wireOp",EDGE,"E1.bottom"),sQuery(id+"F0.wireOp",EDGE,"E1.top"),sQuery(id+"F0.wireOp",EDGE,"E1.left"),sQuery(id+"F0.wireOp",EDGE,"E2"),sQuery(id+"F0.wireOp",EDGE,"E3"),sQuery(id+"F0.wireOp",EDGE,"E4"),sQuery(id+"F0.wireOp",EDGE,"E5"),subQ0,sQuery(id+"F0.wireOp",EDGE,"E7"),sQuery(id+"F0.wireOp",EDGE,"E8")])],"isStart":true})])],"derivedFrom":subQ1}),makeQuery(id+"F5.opExtrude","SWEPT_FACE",FACE,{"disambiguationData":[OSD([sQuery(id+"F4.wireOp",EDGE,"E15")])]})]});}
            var Q22;
            Q22=makeQuery(id+"F5.boolean.opBoolean","INTERSECT",EDGE,{"disambiguationData":[OD(0.0)],"derivedFrom":[makeQuery(id+"F3.boolean.opBoolean","COPY",FACE,{"disambiguationData":[OD(2.0)],"derivedFrom":makeQuery(id+"F3.opExtrude","SWEPT_FACE",FACE,{"disambiguationData":[OSD([sQuery(id+"F2.wireOp",EDGE,"E11")])]})}),makeQuery(id+"F5.opExtrude","SWEPT_FACE",FACE,{"disambiguationData":[OSD([sQuery(id+"F4.wireOp",EDGE,"E15")])]})]});
            var Q23;
            Q23=makeQuery(id+"F5.boolean.opBoolean","INTERSECT",EDGE,{"disambiguationData":[OD(1.0)],"derivedFrom":[makeQuery(id+"F3.boolean.opBoolean","COPY",FACE,{"disambiguationData":[OD(0.0)],"derivedFrom":makeQuery(id+"F3.opExtrude","SWEPT_FACE",FACE,{"disambiguationData":[OSD([sQuery(id+"F2.wireOp",EDGE,"E11")])]})}),makeQuery(id+"F5.opExtrude","SWEPT_FACE",FACE,{"disambiguationData":[OSD([sQuery(id+"F4.wireOp",EDGE,"E15")])]})]});
            var Q24;
            Q24=makeQuery(id+"F3.boolean.opBoolean","INTERSECT",EDGE,{"disambiguationData":[OD(0.0)],"derivedFrom":[makeQuery(id+"F1.opExtrude","SWEPT_FACE",FACE,{"disambiguationData":[OSD([sQuery(id+"F0.wireOp",EDGE,"E7")])]}),makeQuery(id+"F3.opExtrude","SWEPT_FACE",FACE,{"disambiguationData":[OSD([sQuery(id+"F2.wireOp",EDGE,"E11")])]})]});
            var Q25;
            {var subQ0=sQuery(id+"F0.wireOp",EDGE,"E7");var subQ1=makeQuery(id+"F1.opExtrude","SWEPT_FACE",FACE,{"disambiguationData":[OSD([subQ0])]});Q25=makeQuery(id+"F5.boolean.opBoolean","INTERSECT",EDGE,{"disambiguationData":[OD(0.0)],"derivedFrom":[makeQuery(id+"F3.boolean.opBoolean","SPLIT",FACE,{"disambiguationData":[TD([makeQuery(id+"F1.opExtrude","CAP_FACE",FACE,{"disambiguationData":[OSD([sQuery(id+"F0.wireOp",EDGE,"E0.bottom"),sQuery(id+"F0.wireOp",EDGE,"E0.left"),sQuery(id+"F0.wireOp",EDGE,"E1.bottom"),sQuery(id+"F0.wireOp",EDGE,"E1.top"),sQuery(id+"F0.wireOp",EDGE,"E1.left"),sQuery(id+"F0.wireOp",EDGE,"E2"),sQuery(id+"F0.wireOp",EDGE,"E3"),sQuery(id+"F0.wireOp",EDGE,"E4"),sQuery(id+"F0.wireOp",EDGE,"E5"),sQuery(id+"F0.wireOp",EDGE,"E6"),subQ0,sQuery(id+"F0.wireOp",EDGE,"E8")])],"isStart":true})])],"derivedFrom":subQ1}),makeQuery(id+"F5.opExtrude","SWEPT_FACE",FACE,{"disambiguationData":[OSD([sQuery(id+"F4.wireOp",EDGE,"E16")])]})]});}
            var Q26;
            Q26=makeQuery(id+"F5.boolean.opBoolean","INTERSECT",EDGE,{"disambiguationData":[OD(0.0)],"derivedFrom":[makeQuery(id+"F3.boolean.opBoolean","COPY",FACE,{"disambiguationData":[OD(2.0)],"derivedFrom":makeQuery(id+"F3.opExtrude","SWEPT_FACE",FACE,{"disambiguationData":[OSD([sQuery(id+"F2.wireOp",EDGE,"E11")])]})}),makeQuery(id+"F5.opExtrude","SWEPT_FACE",FACE,{"disambiguationData":[OSD([sQuery(id+"F4.wireOp",EDGE,"E16")])]})]});
            var Q27;
            Q27=makeQuery(id+"F3.boolean.opBoolean","INTERSECT",EDGE,{"disambiguationData":[OD(2.0)],"derivedFrom":[makeQuery(id+"F1.opExtrude","SWEPT_FACE",FACE,{"disambiguationData":[OSD([sQuery(id+"F0.wireOp",EDGE,"E7")])]}),makeQuery(id+"F3.opExtrude","SWEPT_FACE",FACE,{"disambiguationData":[OSD([sQuery(id+"F2.wireOp",EDGE,"E11")])]})]});
            var Q28;
            {var subQ0=sQuery(id+"F0.wireOp",EDGE,"E7");var subQ1=makeQuery(id+"F1.opExtrude","SWEPT_FACE",FACE,{"disambiguationData":[OSD([subQ0])]});Q28=makeQuery(id+"F5.boolean.opBoolean","INTERSECT",EDGE,{"disambiguationData":[OD(0.0)],"derivedFrom":[makeQuery(id+"F3.boolean.opBoolean","SPLIT",FACE,{"disambiguationData":[TD([makeQuery(id+"F1.opExtrude","CAP_FACE",FACE,{"disambiguationData":[OSD([sQuery(id+"F0.wireOp",EDGE,"E0.bottom"),sQuery(id+"F0.wireOp",EDGE,"E0.left"),sQuery(id+"F0.wireOp",EDGE,"E1.bottom"),sQuery(id+"F0.wireOp",EDGE,"E1.top"),sQuery(id+"F0.wireOp",EDGE,"E1.left"),sQuery(id+"F0.wireOp",EDGE,"E2"),sQuery(id+"F0.wireOp",EDGE,"E3"),sQuery(id+"F0.wireOp",EDGE,"E4"),sQuery(id+"F0.wireOp",EDGE,"E5"),sQuery(id+"F0.wireOp",EDGE,"E6"),subQ0,sQuery(id+"F0.wireOp",EDGE,"E8")])],"isStart":false})])],"derivedFrom":subQ1}),makeQuery(id+"F5.opExtrude","SWEPT_FACE",FACE,{"disambiguationData":[OSD([sQuery(id+"F4.wireOp",EDGE,"E16")])]})]});}
            var Q29;
            Q29=makeQuery(id+"F5.boolean.opBoolean","INTERSECT",EDGE,{"disambiguationData":[OD(1.0)],"derivedFrom":[makeQuery(id+"F3.boolean.opBoolean","COPY",FACE,{"disambiguationData":[OD(2.0)],"derivedFrom":makeQuery(id+"F3.opExtrude","SWEPT_FACE",FACE,{"disambiguationData":[OSD([sQuery(id+"F2.wireOp",EDGE,"E11")])]})}),makeQuery(id+"F5.opExtrude","SWEPT_FACE",FACE,{"disambiguationData":[OSD([sQuery(id+"F4.wireOp",EDGE,"E16")])]})]});
            var Q30;
            {var subQ0=sQuery(id+"F0.wireOp",EDGE,"E7");var subQ1=makeQuery(id+"F1.opExtrude","SWEPT_FACE",FACE,{"disambiguationData":[OSD([subQ0])]});Q30=makeQuery(id+"F5.boolean.opBoolean","INTERSECT",EDGE,{"disambiguationData":[OD(1.0)],"derivedFrom":[makeQuery(id+"F3.boolean.opBoolean","SPLIT",FACE,{"disambiguationData":[TD([makeQuery(id+"F1.opExtrude","CAP_FACE",FACE,{"disambiguationData":[OSD([sQuery(id+"F0.wireOp",EDGE,"E0.bottom"),sQuery(id+"F0.wireOp",EDGE,"E0.left"),sQuery(id+"F0.wireOp",EDGE,"E1.bottom"),sQuery(id+"F0.wireOp",EDGE,"E1.top"),sQuery(id+"F0.wireOp",EDGE,"E1.left"),sQuery(id+"F0.wireOp",EDGE,"E2"),sQuery(id+"F0.wireOp",EDGE,"E3"),sQuery(id+"F0.wireOp",EDGE,"E4"),sQuery(id+"F0.wireOp",EDGE,"E5"),sQuery(id+"F0.wireOp",EDGE,"E6"),subQ0,sQuery(id+"F0.wireOp",EDGE,"E8")])],"isStart":true})])],"derivedFrom":subQ1}),makeQuery(id+"F5.opExtrude","SWEPT_FACE",FACE,{"disambiguationData":[OSD([sQuery(id+"F4.wireOp",EDGE,"E16")])]})]});}
            var Q31;
            {var subQ0=sQuery(id+"F0.wireOp",EDGE,"E7");var subQ1=makeQuery(id+"F1.opExtrude","SWEPT_FACE",FACE,{"disambiguationData":[OSD([subQ0])]});Q31=makeQuery(id+"F5.boolean.opBoolean","INTERSECT",EDGE,{"disambiguationData":[OD(1.0)],"derivedFrom":[makeQuery(id+"F3.boolean.opBoolean","SPLIT",FACE,{"disambiguationData":[TD([makeQuery(id+"F1.opExtrude","CAP_FACE",FACE,{"disambiguationData":[OSD([sQuery(id+"F0.wireOp",EDGE,"E0.bottom"),sQuery(id+"F0.wireOp",EDGE,"E0.left"),sQuery(id+"F0.wireOp",EDGE,"E1.bottom"),sQuery(id+"F0.wireOp",EDGE,"E1.top"),sQuery(id+"F0.wireOp",EDGE,"E1.left"),sQuery(id+"F0.wireOp",EDGE,"E2"),sQuery(id+"F0.wireOp",EDGE,"E3"),sQuery(id+"F0.wireOp",EDGE,"E4"),sQuery(id+"F0.wireOp",EDGE,"E5"),sQuery(id+"F0.wireOp",EDGE,"E6"),subQ0,sQuery(id+"F0.wireOp",EDGE,"E8")])],"isStart":false})])],"derivedFrom":subQ1}),makeQuery(id+"F5.opExtrude","SWEPT_FACE",FACE,{"disambiguationData":[OSD([sQuery(id+"F4.wireOp",EDGE,"E16")])]})]});}
            var Q32;
            Q32=makeQuery(id+"F5.boolean.opBoolean","INTERSECT",EDGE,{"disambiguationData":[OD(1.0)],"derivedFrom":[makeQuery(id+"F3.boolean.opBoolean","COPY",FACE,{"disambiguationData":[OD(3.0)],"derivedFrom":makeQuery(id+"F3.opExtrude","SWEPT_FACE",FACE,{"disambiguationData":[OSD([sQuery(id+"F2.wireOp",EDGE,"E11")])]})}),makeQuery(id+"F5.opExtrude","SWEPT_FACE",FACE,{"disambiguationData":[OSD([sQuery(id+"F4.wireOp",EDGE,"E16")])]})]});
            var Q33;
            Q33=makeQuery(id+"F3.boolean.opBoolean","INTERSECT",EDGE,{"disambiguationData":[OD(1.0)],"derivedFrom":[makeQuery(id+"F1.opExtrude","SWEPT_FACE",FACE,{"disambiguationData":[OSD([sQuery(id+"F0.wireOp",EDGE,"E7")])]}),makeQuery(id+"F3.opExtrude","SWEPT_FACE",FACE,{"disambiguationData":[OSD([sQuery(id+"F2.wireOp",EDGE,"E11")])]})]});
            var Q34;
            Q34=makeQuery(id+"F5.boolean.opBoolean","INTERSECT",EDGE,{"disambiguationData":[OD(0.0)],"derivedFrom":[makeQuery(id+"F3.boolean.opBoolean","COPY",FACE,{"disambiguationData":[OD(3.0)],"derivedFrom":makeQuery(id+"F3.opExtrude","SWEPT_FACE",FACE,{"disambiguationData":[OSD([sQuery(id+"F2.wireOp",EDGE,"E11")])]})}),makeQuery(id+"F5.opExtrude","SWEPT_FACE",FACE,{"disambiguationData":[OSD([sQuery(id+"F4.wireOp",EDGE,"E16")])]})]});
            var Q35;
            Q35=makeQuery(id+"F3.boolean.opBoolean","INTERSECT",EDGE,{"disambiguationData":[OD(3.0)],"derivedFrom":[makeQuery(id+"F1.opExtrude","SWEPT_FACE",FACE,{"disambiguationData":[OSD([sQuery(id+"F0.wireOp",EDGE,"E7")])]}),makeQuery(id+"F3.opExtrude","SWEPT_FACE",FACE,{"disambiguationData":[OSD([sQuery(id+"F2.wireOp",EDGE,"E11")])]})]});
            var Q36;
            Q36=makeQuery(id+"F5.boolean.opBoolean","INTERSECT",EDGE,{"disambiguationData":[OD(1.0)],"derivedFrom":[makeQuery(id+"F3.boolean.opBoolean","COPY",FACE,{"disambiguationData":[OD(3.0)],"derivedFrom":makeQuery(id+"F3.opExtrude","SWEPT_FACE",FACE,{"disambiguationData":[OSD([sQuery(id+"F2.wireOp",EDGE,"E11")])]})}),makeQuery(id+"F5.opExtrude","SWEPT_FACE",FACE,{"disambiguationData":[OSD([sQuery(id+"F4.wireOp",EDGE,"E17")])]})]});
            var Q37;
            {var subQ0=sQuery(id+"F0.wireOp",EDGE,"E8");var subQ1=makeQuery(id+"F1.opExtrude","SWEPT_FACE",FACE,{"disambiguationData":[OSD([subQ0])]});Q37=makeQuery(id+"F5.boolean.opBoolean","INTERSECT",EDGE,{"disambiguationData":[OD(1.0)],"derivedFrom":[makeQuery(id+"F3.boolean.opBoolean","SPLIT",FACE,{"disambiguationData":[TD([makeQuery(id+"F1.opExtrude","CAP_FACE",FACE,{"disambiguationData":[OSD([sQuery(id+"F0.wireOp",EDGE,"E0.bottom"),sQuery(id+"F0.wireOp",EDGE,"E0.left"),sQuery(id+"F0.wireOp",EDGE,"E1.bottom"),sQuery(id+"F0.wireOp",EDGE,"E1.top"),sQuery(id+"F0.wireOp",EDGE,"E1.left"),sQuery(id+"F0.wireOp",EDGE,"E2"),sQuery(id+"F0.wireOp",EDGE,"E3"),sQuery(id+"F0.wireOp",EDGE,"E4"),sQuery(id+"F0.wireOp",EDGE,"E5"),sQuery(id+"F0.wireOp",EDGE,"E6"),sQuery(id+"F0.wireOp",EDGE,"E7"),subQ0])],"isStart":false})])],"derivedFrom":subQ1}),makeQuery(id+"F5.opExtrude","SWEPT_FACE",FACE,{"disambiguationData":[OSD([sQuery(id+"F4.wireOp",EDGE,"E17")])]})]});}
            var Q38;
            Q38=makeQuery(id+"F3.boolean.opBoolean","INTERSECT",EDGE,{"disambiguationData":[OD(3.0)],"derivedFrom":[makeQuery(id+"F1.opExtrude","SWEPT_FACE",FACE,{"disambiguationData":[OSD([sQuery(id+"F0.wireOp",EDGE,"E8")])]}),makeQuery(id+"F3.opExtrude","SWEPT_FACE",FACE,{"disambiguationData":[OSD([sQuery(id+"F2.wireOp",EDGE,"E11")])]})]});
            var Q39;
            Q39=makeQuery(id+"F3.boolean.opBoolean","INTERSECT",EDGE,{"disambiguationData":[OD(2.0)],"derivedFrom":[makeQuery(id+"F1.opExtrude","SWEPT_FACE",FACE,{"disambiguationData":[OSD([sQuery(id+"F0.wireOp",EDGE,"E8")])]}),makeQuery(id+"F3.opExtrude","SWEPT_FACE",FACE,{"disambiguationData":[OSD([sQuery(id+"F2.wireOp",EDGE,"E11")])]})]});
            var Q40;
            {var subQ0=sQuery(id+"F0.wireOp",EDGE,"E8");var subQ1=makeQuery(id+"F1.opExtrude","SWEPT_FACE",FACE,{"disambiguationData":[OSD([subQ0])]});Q40=makeQuery(id+"F5.boolean.opBoolean","INTERSECT",EDGE,{"disambiguationData":[OD(1.0)],"derivedFrom":[makeQuery(id+"F3.boolean.opBoolean","SPLIT",FACE,{"disambiguationData":[TD([makeQuery(id+"F1.opExtrude","CAP_FACE",FACE,{"disambiguationData":[OSD([sQuery(id+"F0.wireOp",EDGE,"E0.bottom"),sQuery(id+"F0.wireOp",EDGE,"E0.left"),sQuery(id+"F0.wireOp",EDGE,"E1.bottom"),sQuery(id+"F0.wireOp",EDGE,"E1.top"),sQuery(id+"F0.wireOp",EDGE,"E1.left"),sQuery(id+"F0.wireOp",EDGE,"E2"),sQuery(id+"F0.wireOp",EDGE,"E3"),sQuery(id+"F0.wireOp",EDGE,"E4"),sQuery(id+"F0.wireOp",EDGE,"E5"),sQuery(id+"F0.wireOp",EDGE,"E6"),sQuery(id+"F0.wireOp",EDGE,"E7"),subQ0])],"isStart":true})])],"derivedFrom":subQ1}),makeQuery(id+"F5.opExtrude","SWEPT_FACE",FACE,{"disambiguationData":[OSD([sQuery(id+"F4.wireOp",EDGE,"E17")])]})]});}
            var Q41;
            Q41=makeQuery(id+"F3.boolean.opBoolean","INTERSECT",EDGE,{"disambiguationData":[OD(0.0)],"derivedFrom":[makeQuery(id+"F1.opExtrude","SWEPT_FACE",FACE,{"disambiguationData":[OSD([sQuery(id+"F0.wireOp",EDGE,"E8")])]}),makeQuery(id+"F3.opExtrude","SWEPT_FACE",FACE,{"disambiguationData":[OSD([sQuery(id+"F2.wireOp",EDGE,"E11")])]})]});
            var Q42;
            {var subQ0=sQuery(id+"F0.wireOp",EDGE,"E8");var subQ1=makeQuery(id+"F1.opExtrude","SWEPT_FACE",FACE,{"disambiguationData":[OSD([subQ0])]});Q42=makeQuery(id+"F5.boolean.opBoolean","INTERSECT",EDGE,{"disambiguationData":[OD(0.0)],"derivedFrom":[makeQuery(id+"F3.boolean.opBoolean","SPLIT",FACE,{"disambiguationData":[TD([makeQuery(id+"F1.opExtrude","CAP_FACE",FACE,{"disambiguationData":[OSD([sQuery(id+"F0.wireOp",EDGE,"E0.bottom"),sQuery(id+"F0.wireOp",EDGE,"E0.left"),sQuery(id+"F0.wireOp",EDGE,"E1.bottom"),sQuery(id+"F0.wireOp",EDGE,"E1.top"),sQuery(id+"F0.wireOp",EDGE,"E1.left"),sQuery(id+"F0.wireOp",EDGE,"E2"),sQuery(id+"F0.wireOp",EDGE,"E3"),sQuery(id+"F0.wireOp",EDGE,"E4"),sQuery(id+"F0.wireOp",EDGE,"E5"),sQuery(id+"F0.wireOp",EDGE,"E6"),sQuery(id+"F0.wireOp",EDGE,"E7"),subQ0])],"isStart":true})])],"derivedFrom":subQ1}),makeQuery(id+"F5.opExtrude","SWEPT_FACE",FACE,{"disambiguationData":[OSD([sQuery(id+"F4.wireOp",EDGE,"E17")])]})]});}
            var Q43;
            Q43=makeQuery(id+"F5.boolean.opBoolean","INTERSECT",EDGE,{"disambiguationData":[OD(0.0)],"derivedFrom":[makeQuery(id+"F3.boolean.opBoolean","COPY",FACE,{"disambiguationData":[OD(3.0)],"derivedFrom":makeQuery(id+"F3.opExtrude","SWEPT_FACE",FACE,{"disambiguationData":[OSD([sQuery(id+"F2.wireOp",EDGE,"E11")])]})}),makeQuery(id+"F5.opExtrude","SWEPT_FACE",FACE,{"disambiguationData":[OSD([sQuery(id+"F4.wireOp",EDGE,"E17")])]})]});
            var Q44;
            Q44=makeQuery(id+"F5.boolean.opBoolean","INTERSECT",EDGE,{"disambiguationData":[OD(1.0)],"derivedFrom":[makeQuery(id+"F3.boolean.opBoolean","COPY",FACE,{"disambiguationData":[OD(1.0)],"derivedFrom":makeQuery(id+"F3.opExtrude","SWEPT_FACE",FACE,{"disambiguationData":[OSD([sQuery(id+"F2.wireOp",EDGE,"E11")])]})}),makeQuery(id+"F5.opExtrude","SWEPT_FACE",FACE,{"disambiguationData":[OSD([sQuery(id+"F4.wireOp",EDGE,"E17")])]})]});
            var Q45;
            Q45=makeQuery(id+"F5.boolean.opBoolean","INTERSECT",EDGE,{"disambiguationData":[OD(0.0)],"derivedFrom":[makeQuery(id+"F3.boolean.opBoolean","COPY",FACE,{"disambiguationData":[OD(1.0)],"derivedFrom":makeQuery(id+"F3.opExtrude","SWEPT_FACE",FACE,{"disambiguationData":[OSD([sQuery(id+"F2.wireOp",EDGE,"E11")])]})}),makeQuery(id+"F5.opExtrude","SWEPT_FACE",FACE,{"disambiguationData":[OSD([sQuery(id+"F4.wireOp",EDGE,"E17")])]})]});
            var Q46;
            Q46=makeQuery(id+"F3.boolean.opBoolean","INTERSECT",EDGE,{"disambiguationData":[OD(1.0)],"derivedFrom":[makeQuery(id+"F1.opExtrude","SWEPT_FACE",FACE,{"disambiguationData":[OSD([sQuery(id+"F0.wireOp",EDGE,"E8")])]}),makeQuery(id+"F3.opExtrude","SWEPT_FACE",FACE,{"disambiguationData":[OSD([sQuery(id+"F2.wireOp",EDGE,"E11")])]})]});
            var Q47;
            {var subQ0=sQuery(id+"F0.wireOp",EDGE,"E8");var subQ1=makeQuery(id+"F1.opExtrude","SWEPT_FACE",FACE,{"disambiguationData":[OSD([subQ0])]});Q47=makeQuery(id+"F5.boolean.opBoolean","INTERSECT",EDGE,{"disambiguationData":[OD(0.0)],"derivedFrom":[makeQuery(id+"F3.boolean.opBoolean","SPLIT",FACE,{"disambiguationData":[TD([makeQuery(id+"F1.opExtrude","CAP_FACE",FACE,{"disambiguationData":[OSD([sQuery(id+"F0.wireOp",EDGE,"E0.bottom"),sQuery(id+"F0.wireOp",EDGE,"E0.left"),sQuery(id+"F0.wireOp",EDGE,"E1.bottom"),sQuery(id+"F0.wireOp",EDGE,"E1.top"),sQuery(id+"F0.wireOp",EDGE,"E1.left"),sQuery(id+"F0.wireOp",EDGE,"E2"),sQuery(id+"F0.wireOp",EDGE,"E3"),sQuery(id+"F0.wireOp",EDGE,"E4"),sQuery(id+"F0.wireOp",EDGE,"E5"),sQuery(id+"F0.wireOp",EDGE,"E6"),sQuery(id+"F0.wireOp",EDGE,"E7"),subQ0])],"isStart":false})])],"derivedFrom":subQ1}),makeQuery(id+"F5.opExtrude","SWEPT_FACE",FACE,{"disambiguationData":[OSD([sQuery(id+"F4.wireOp",EDGE,"E17")])]})]});}
            fillet(context, id + "F8", {"entities" : qUnion([Q0, Q1, Q2, Q3, Q4, Q5, Q6, Q7, Q8, Q9, Q10, Q11, Q12, Q13, Q14, Q15, Q16, Q17, Q18, Q19, Q20, Q21, Q22, Q23, Q24, Q25, Q26, Q27, Q28, Q29, Q30, Q31, Q32, Q33, Q34, Q35, Q36, Q37, Q38, Q39, Q40, Q41, Q42, Q43, Q44, Q45, Q46, Q47]), "radius" : 2.54 * mm, "tangentPropagation" : true, "allowEdgeOverflow" : false});
        }
        {
            var Q0;
            Q0=makeQuery(id+"F1.opExtrude","CAP_EDGE",EDGE,{"disambiguationData":[OSD([sQuery(id+"F0.wireOp",EDGE,"E6")])],"isStart":false});
            var Q1;
            Q1=makeQuery(id+"F1.opExtrude","CAP_EDGE",EDGE,{"disambiguationData":[OSD([sQuery(id+"F0.wireOp",EDGE,"E5")])],"isStart":false});
            var Q2;
            Q2=makeQuery(id+"F1.opExtrude","CAP_EDGE",EDGE,{"disambiguationData":[OSD([sQuery(id+"F0.wireOp",EDGE,"E4")])],"isStart":false});
            var Q3;
            Q3=makeQuery(id+"F1.opExtrude","CAP_EDGE",EDGE,{"disambiguationData":[OSD([sQuery(id+"F0.wireOp",EDGE,"E7")])],"isStart":false});
            var Q4;
            Q4=makeQuery(id+"F1.opExtrude","CAP_EDGE",EDGE,{"disambiguationData":[OSD([sQuery(id+"F0.wireOp",EDGE,"E8")])],"isStart":false});
            var Q5;
            Q5=makeQuery(id+"F3.boolean.opBoolean","COPY",EDGE,{"derivedFrom":makeQuery(id+"F3.opExtrude","CAP_EDGE",EDGE,{"disambiguationData":[OSD([sQuery(id+"F2.wireOp",EDGE,"E11")])],"isStart":false})});
            var Q6;
            Q6=makeQuery(id+"F3.boolean.opBoolean","INTERSECT",EDGE,{"derivedFrom":[makeQuery(id+"F1.opExtrude","SWEPT_FACE",FACE,{"disambiguationData":[OSD([sQuery(id+"F0.wireOp",EDGE,"E3")])]}),makeQuery(id+"F3.opExtrude","SWEPT_FACE",FACE,{"disambiguationData":[OSD([sQuery(id+"F2.wireOp",EDGE,"E10")])]})]});
            var Q7;
            Q7=makeQuery(id+"F3.boolean.opBoolean","INTERSECT",EDGE,{"derivedFrom":[makeQuery(id+"F1.opExtrude","SWEPT_FACE",FACE,{"disambiguationData":[OSD([sQuery(id+"F0.wireOp",EDGE,"E3")])]}),makeQuery(id+"F3.opExtrude","SWEPT_FACE",FACE,{"disambiguationData":[OSD([sQuery(id+"F2.wireOp",EDGE,"E9")])]})]});
            var Q8;
            Q8=makeQuery(id+"F5.boolean.opBoolean","INTERSECT",EDGE,{"derivedFrom":[makeQuery(id+"F1.opExtrude","SWEPT_FACE",FACE,{"disambiguationData":[OSD([sQuery(id+"F0.wireOp",EDGE,"E2")])]}),makeQuery(id+"F5.opExtrude","SWEPT_FACE",FACE,{"disambiguationData":[OSD([sQuery(id+"F4.wireOp",EDGE,"E17")])]})]});
            var Q9;
            Q9=makeQuery(id+"F5.boolean.opBoolean","INTERSECT",EDGE,{"derivedFrom":[makeQuery(id+"F1.opExtrude","SWEPT_FACE",FACE,{"disambiguationData":[OSD([sQuery(id+"F0.wireOp",EDGE,"E2")])]}),makeQuery(id+"F5.opExtrude","SWEPT_FACE",FACE,{"disambiguationData":[OSD([sQuery(id+"F4.wireOp",EDGE,"E16")])]})]});
            var Q10;
            Q10=makeQuery(id+"F5.boolean.opBoolean","COPY",EDGE,{"derivedFrom":makeQuery(id+"F5.opExtrude","CAP_EDGE",EDGE,{"disambiguationData":[OSD([sQuery(id+"F4.wireOp",EDGE,"E15")])],"isStart":false})});
            var Q11;
            Q11=makeQuery(id+"F1.opExtrude","CAP_EDGE",EDGE,{"disambiguationData":[OSD([sQuery(id+"F0.wireOp",EDGE,"E4")])],"isStart":true});
            var Q12;
            Q12=makeQuery(id+"F1.opExtrude","CAP_EDGE",EDGE,{"disambiguationData":[OSD([sQuery(id+"F0.wireOp",EDGE,"E5")])],"isStart":true});
            var Q13;
            Q13=makeQuery(id+"F1.opExtrude","CAP_EDGE",EDGE,{"disambiguationData":[OSD([sQuery(id+"F0.wireOp",EDGE,"E6")])],"isStart":true});
            var Q14;
            Q14=makeQuery(id+"F1.opExtrude","CAP_EDGE",EDGE,{"disambiguationData":[OSD([sQuery(id+"F0.wireOp",EDGE,"E7")])],"isStart":true});
            var Q15;
            Q15=makeQuery(id+"F1.opExtrude","CAP_EDGE",EDGE,{"disambiguationData":[OSD([sQuery(id+"F0.wireOp",EDGE,"E8")])],"isStart":true});
            var Q16;
            Q16=makeQuery(id+"F3.boolean.opBoolean","COPY",EDGE,{"derivedFrom":makeQuery(id+"F3.opExtrude","CAP_EDGE",EDGE,{"disambiguationData":[OSD([sQuery(id+"F2.wireOp",EDGE,"E11")])],"isStart":true})});
            var Q17;
            Q17=makeQuery(id+"F3.boolean.opBoolean","COPY",EDGE,{"derivedFrom":makeQuery(id+"F3.opExtrude","CAP_EDGE",EDGE,{"disambiguationData":[OSD([sQuery(id+"F2.wireOp",EDGE,"E10")])],"isStart":true})});
            var Q18;
            Q18=makeQuery(id+"F3.boolean.opBoolean","COPY",EDGE,{"derivedFrom":makeQuery(id+"F3.opExtrude","CAP_EDGE",EDGE,{"disambiguationData":[OSD([sQuery(id+"F2.wireOp",EDGE,"E9")])],"isStart":true})});
            var Q19;
            Q19=makeQuery(id+"F5.boolean.opBoolean","COPY",EDGE,{"derivedFrom":makeQuery(id+"F5.opExtrude","CAP_EDGE",EDGE,{"disambiguationData":[OSD([sQuery(id+"F4.wireOp",EDGE,"E15")])],"isStart":true})});
            var Q20;
            Q20=makeQuery(id+"F5.boolean.opBoolean","COPY",EDGE,{"derivedFrom":makeQuery(id+"F5.opExtrude","CAP_EDGE",EDGE,{"disambiguationData":[OSD([sQuery(id+"F4.wireOp",EDGE,"E16")])],"isStart":true})});
            var Q21;
            Q21=makeQuery(id+"F5.boolean.opBoolean","COPY",EDGE,{"derivedFrom":makeQuery(id+"F5.opExtrude","CAP_EDGE",EDGE,{"disambiguationData":[OSD([sQuery(id+"F4.wireOp",EDGE,"E17")])],"isStart":true})});
            fillet(context, id + "F9", {"entities" : qUnion([Q0, Q1, Q2, Q3, Q4, Q5, Q6, Q7, Q8, Q9, Q10, Q11, Q12, Q13, Q14, Q15, Q16, Q17, Q18, Q19, Q20, Q21]), "radius" : 2.54 * mm, "tangentPropagation" : true, "allowEdgeOverflow" : false});
        }
    });
